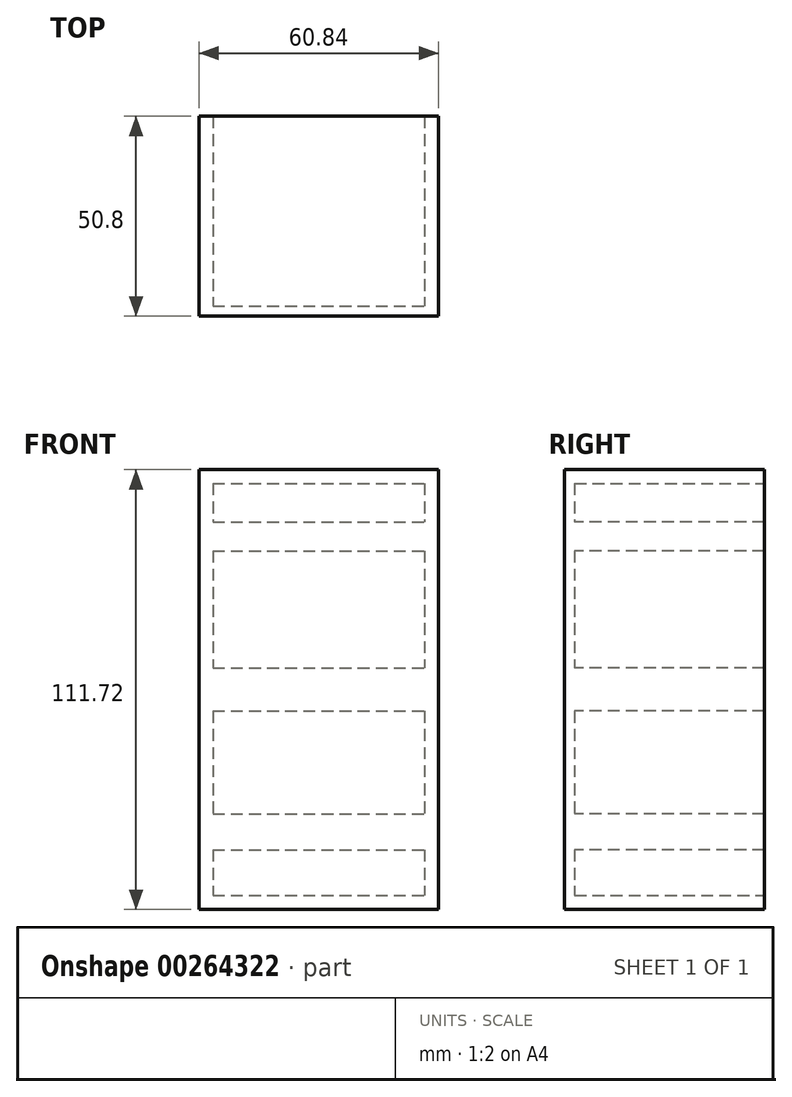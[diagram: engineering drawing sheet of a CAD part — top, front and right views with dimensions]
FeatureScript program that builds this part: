
annotation { "Feature Type Name" : "Feature", "Feature Type Description" : "" }
export const myFeature = defineFeature(function(context is Context, id is Id, definition is map)
    precondition{}
    {
        {
            var Q0;
            Q0=qCreatedBy(makeId("Front.planeOp"),FACE);
            var sketch = newSketch(context, id + "F0", { "sketchPlane" : qUnion([Q0])});
            skLineSegment(sketch, "E0.bottom", {"start": v(30.42, 55.86) * mm, "end": v(-30.42, 55.86) * mm});
            skLineSegment(sketch, "E0.top", {"start": v(30.42, -55.86) * mm, "end": v(-30.42, -55.86) * mm});
            skLineSegment(sketch, "E0.left", {"start": v(30.42, 55.86) * mm, "end": v(30.42, -55.86) * mm});
            skLineSegment(sketch, "E0.right", {"start": v(-30.42, 55.86) * mm, "end": v(-30.42, -55.86) * mm});
            skPoint(sketch, "E0.middle", {"position": v(0, 0) * mm});
            skSolve(sketch);
        }
        {
            var Q0;
            Q0 = qSketchRegion(id + "F0", true);
            extrude(context, id + "F1", {"entities" : qUnion([Q0]), "depth" : 50.8 * mm});
        }
        {
            var Q0;
            Q0=qCreatedBy(makeId("Front.planeOp"),FACE);
            var sketch = newSketch(context, id + "F2", { "sketchPlane" : qUnion([Q0])});
            skLineSegment(sketch, "E1.bottom", {"start": v(-26.92, 52.36) * mm, "end": v(26.92, 52.36) * mm});
            skLineSegment(sketch, "E1.top", {"start": v(-26.92, -52.36) * mm, "end": v(26.92, -52.36) * mm});
            skLineSegment(sketch, "E1.left", {"start": v(-26.92, 52.36) * mm, "end": v(-26.92, -52.36) * mm});
            skLineSegment(sketch, "E1.right", {"start": v(26.92, 52.36) * mm, "end": v(26.92, -52.36) * mm});
            skPoint(sketch, "E1.middle", {"position": v(0, 0) * mm});
            skSolve(sketch);
        }
        {
            var Q0;
            Q0 = qSketchRegion(id + "F2", true);
            extrude(context, id + "F3", {"entities" : qUnion([Q0]), "operationType" : NewBodyOperationType.REMOVE, "depth" : 48.26 * mm});
        }
        {
            var Q0;
            Q0=qCreatedBy(makeId("Front.planeOp"),FACE);
            var sketch = newSketch(context, id + "F4", { "sketchPlane" : qUnion([Q0])});
            skLineSegment(sketch, "E2.bottom", {"start": v(-27.76, 35.25) * mm, "end": v(24.3, 35.25) * mm});
            skLineSegment(sketch, "E2.top", {"start": v(-27.76, 42.51) * mm, "end": v(24.3, 42.51) * mm});
            skLineSegment(sketch, "E2.left", {"start": v(-27.76, 35.25) * mm, "end": v(-27.76, 42.51) * mm});
            skLineSegment(sketch, "E2.right", {"start": v(24.3, 35.25) * mm, "end": v(24.3, 42.51) * mm});
            skPoint(sketch, "E2.middle", {"position": v(-1.73, 38.88) * mm});
            skLineSegment(sketch, "E3.bottom", {"start": v(-27.23, 5.46) * mm, "end": v(27.23, 5.46) * mm});
            skLineSegment(sketch, "E3.top", {"start": v(-27.23, -5.46) * mm, "end": v(27.23, -5.46) * mm});
            skLineSegment(sketch, "E3.left", {"start": v(-27.23, 5.46) * mm, "end": v(-27.23, -5.46) * mm});
            skLineSegment(sketch, "E3.right", {"start": v(27.23, 5.46) * mm, "end": v(27.23, -5.46) * mm});
            skPoint(sketch, "E3.middle", {"position": v(0, 0) * mm});
            skLineSegment(sketch, "E4.bottom", {"start": v(-27.23, -31.66) * mm, "end": v(27.23, -31.66) * mm});
            skLineSegment(sketch, "E4.top", {"start": v(-27.23, -40.72) * mm, "end": v(27.23, -40.72) * mm});
            skLineSegment(sketch, "E4.left", {"start": v(-27.23, -31.66) * mm, "end": v(-27.23, -40.72) * mm});
            skLineSegment(sketch, "E4.right", {"start": v(27.23, -31.66) * mm, "end": v(27.23, -40.72) * mm});
            skPoint(sketch, "E4.middle", {"position": v(0, -36.2) * mm});
            skSolve(sketch);
        }
        {
            var Q0;
            Q0 = qSketchRegion(id + "F4", true);
            extrude(context, id + "F5", {"entities" : qUnion([Q0]), "operationType" : NewBodyOperationType.ADD, "depth" : 48.26 * mm});
        }
        {
            var Q0;
            Q0=makeQuery(id+"F5.opExtrude","SWEPT_FACE",FACE,{"disambiguationData":[OSD([sQuery(id+"F4.wireOp",EDGE,"E2.right")])]});
            extrude(context, id + "F6", {"entities" : qUnion([Q0]), "operationType" : NewBodyOperationType.ADD, "depth" : 5.08 * mm});
        }
    });
